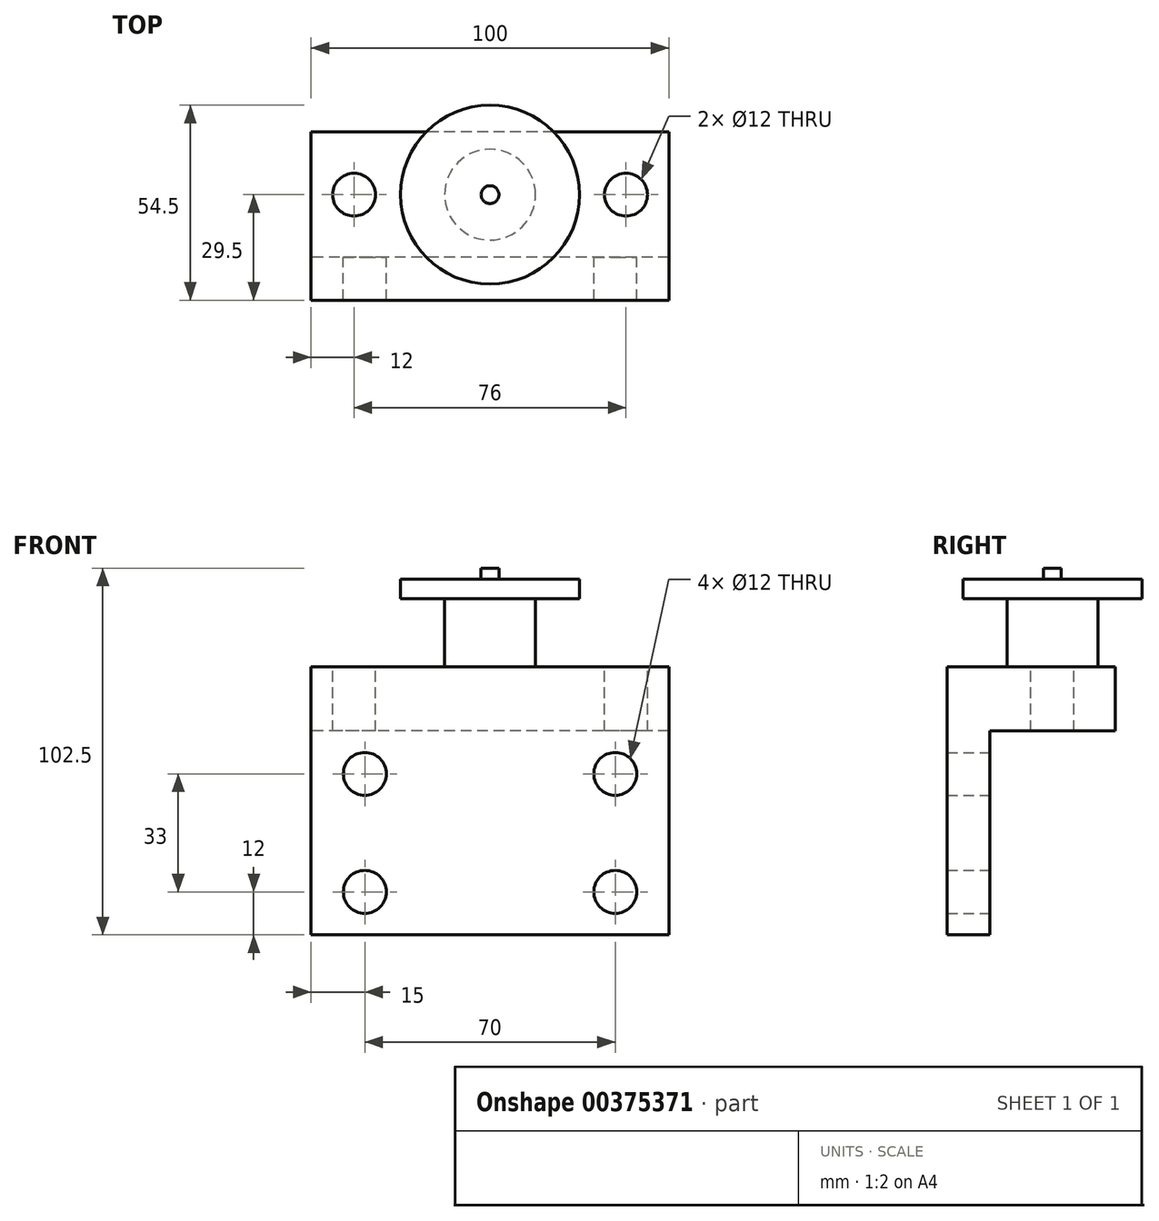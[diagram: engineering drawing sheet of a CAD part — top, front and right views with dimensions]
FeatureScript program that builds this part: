
annotation { "Feature Type Name" : "Feature", "Feature Type Description" : "" }
export const myFeature = defineFeature(function(context is Context, id is Id, definition is map)
    precondition{}
    {
        {
            var Q0;
            Q0=qCreatedBy(makeId("Top.planeOp"),FACE);
            var sketch = newSketch(context, id + "F0", { "sketchPlane" : qUnion([Q0])});
            skLineSegment(sketch, "E0.bottom", {"start": v(50, -17.5) * mm, "end": v(-50, -17.5) * mm});
            skLineSegment(sketch, "E0.top", {"start": v(50, 17.5) * mm, "end": v(-50, 17.5) * mm});
            skLineSegment(sketch, "E0.left", {"start": v(50, -17.5) * mm, "end": v(50, 17.5) * mm});
            skLineSegment(sketch, "E0.right", {"start": v(-50, -17.5) * mm, "end": v(-50, 17.5) * mm});
            skPoint(sketch, "E0.middle", {"position": v(0, 0) * mm});
            skSolve(sketch);
        }
        {
            var Q0;
            Q0=makeQuery(id+"F0.imprint","IMPRINT",FACE,{"disambiguationData":[TD([[makeQuery(id+"F0.imprint","IMPRINT",EDGE,{"derivedFrom":sQuery(id+"F0.wireOp",EDGE,"E0.bottom")}),-1.0]])]});
            extrude(context, id + "F1", {"entities" : qUnion([Q0]), "depth" : -18 * mm});
        }
        {
            var Q0;
            Q0=makeQuery(id+"F1.opExtrude","CAP_FACE",FACE,{"disambiguationData":[OSD([sQuery(id+"F0.wireOp",EDGE,"E0.bottom"),sQuery(id+"F0.wireOp",EDGE,"E0.top"),sQuery(id+"F0.wireOp",EDGE,"E0.left"),sQuery(id+"F0.wireOp",EDGE,"E0.right")])],"isStart":true});
            var sketch = newSketch(context, id + "F2", { "sketchPlane" : qUnion([Q0])});
            skLineSegment(sketch, "E1", {"start": v(50, 0) * mm, "end": v(38, 0) * mm, "construction": true});
            skLineSegment(sketch, "E2", {"start": v(-50, 0) * mm, "end": v(-38, 0) * mm, "construction": true});
            skCircle(sketch, "E3", {"center": v(38, 0) * mm, "radius": 6 * mm});
            skCircle(sketch, "E4", {"center": v(-38, 0) * mm, "radius": 6 * mm});
            skSolve(sketch);
        }
        {
            var Q0;
            Q0=sQuery(id+"F2.wireOp",VERTEX,"E2.end");
            var Q1;
            Q1=sQuery(id+"F2.wireOp",VERTEX,"E3.center");
            var Q2;
            Q2=makeQuery(id+"F1.opExtrude","SWEPT_BODY",BODY,{"disambiguationData":[OSD([sQuery(id+"F0.wireOp",EDGE,"E0.bottom"),sQuery(id+"F0.wireOp",EDGE,"E0.top"),sQuery(id+"F0.wireOp",EDGE,"E0.left"),sQuery(id+"F0.wireOp",EDGE,"E0.right")])]});
            hole(context, id + "F3", {"style" : HoleStyle.SIMPLE, "endStyle" : HoleEndStyle.THROUGH, "holeDiameter" : 12 * mm, "isTappedThrough" : true, "tappedDepth" : 12 * mm, "tapClearance" : 3, "locations" : qUnion([Q0, Q1]), "scope" : qUnion([Q2])});
        }
        {
            var Q0;
            Q0=makeQuery(id+"F1.opExtrude","CAP_FACE",FACE,{"disambiguationData":[OSD([sQuery(id+"F0.wireOp",EDGE,"E0.bottom"),sQuery(id+"F0.wireOp",EDGE,"E0.top"),sQuery(id+"F0.wireOp",EDGE,"E0.left"),sQuery(id+"F0.wireOp",EDGE,"E0.right")])],"isStart":true});
            var sketch = newSketch(context, id + "F4", { "sketchPlane" : qUnion([Q0])});
            skCircle(sketch, "E5", {"center": v(0, 0) * mm, "radius": 12.7 * mm});
            skSolve(sketch);
        }
        {
            var Q0;
            Q0=makeQuery(id+"F4.imprint","IMPRINT",FACE,{"disambiguationData":[TD([[makeQuery(id+"F4.imprint","IMPRINT",EDGE,{"derivedFrom":sQuery(id+"F4.wireOp",EDGE,"E5")}),1.0]])]});
            extrude(context, id + "F5", {"entities" : qUnion([Q0]), "operationType" : NewBodyOperationType.ADD, "depth" : 19 * mm});
        }
        {
            var Q0;
            Q0=makeQuery(id+"F5.opExtrude","CAP_FACE",FACE,{"disambiguationData":[OSD([sQuery(id+"F4.wireOp",EDGE,"E5")])],"isStart":false});
            var sketch = newSketch(context, id + "F6", { "sketchPlane" : qUnion([Q0])});
            skCircle(sketch, "E6", {"center": v(0, 0) * mm, "radius": 25 * mm});
            skSolve(sketch);
        }
        {
            var Q0;
            Q0=makeQuery(id+"F6.imprint","IMPRINT",FACE,{"disambiguationData":[TD([[makeQuery(id+"F6.imprint","IMPRINT",EDGE,{"derivedFrom":sQuery(id+"F6.wireOp",EDGE,"E6")}),1.0]])]});
            var Q1;
            Q1=makeQuery(id+"F6.imprint","IMPRINT",FACE,{"disambiguationData":[TD([[makeQuery(id+"F6.imprint","IMPRINT",EDGE,{"derivedFrom":makeQuery(id+"F5.opExtrude","CAP_EDGE",EDGE,{"disambiguationData":[OSD([sQuery(id+"F4.wireOp",EDGE,"E5")])],"isStart":false})}),1.0]])]});
            extrude(context, id + "F7", {"entities" : qUnion([Q0, Q1]), "operationType" : NewBodyOperationType.ADD, "depth" : 5.5 * mm});
        }
        {
            var Q0;
            Q0=makeQuery(id+"F7.opExtrude","CAP_FACE",FACE,{"disambiguationData":[OSD([sQuery(id+"F6.wireOp",EDGE,"E6")])],"isStart":false});
            var sketch = newSketch(context, id + "F8", { "sketchPlane" : qUnion([Q0])});
            skCircle(sketch, "E7", {"center": v(0, 0) * mm, "radius": 2.5 * mm});
            skSolve(sketch);
        }
        {
            var Q0;
            Q0=qSketchRegion(id+"F8",true);
            extrude(context, id + "F9", {"entities" : qUnion([Q0]), "operationType" : NewBodyOperationType.ADD, "depth" : 3 * mm});
        }
        {
            var Q0;
            Q0=makeQuery(id+"F1.opExtrude","SWEPT_FACE",FACE,{"disambiguationData":[OSD([sQuery(id+"F0.wireOp",EDGE,"E0.bottom")])]});
            var sketch = newSketch(context, id + "F10", { "sketchPlane" : qUnion([Q0])});
            skLineSegment(sketch, "E8.bottom", {"start": v(-50, 0) * mm, "end": v(50, 0) * mm});
            skLineSegment(sketch, "E8.top", {"start": v(-50, -75) * mm, "end": v(50, -75) * mm});
            skLineSegment(sketch, "E8.left", {"start": v(-50, 0) * mm, "end": v(-50, -75) * mm});
            skLineSegment(sketch, "E8.right", {"start": v(50, 0) * mm, "end": v(50, -75) * mm});
            skSolve(sketch);
        }
        {
            var Q0;
            {var subQ0=sQuery(id+"F10.wireOp",EDGE,"E8.top");Q0=makeQuery(id+"F10.imprint","IMPRINT",FACE,{"disambiguationData":[TD([[makeQuery(id+"F10.imprint","IMPRINT",EDGE,{"derivedFrom":subQ0}),1.0]])]});}
            var Q1;
            {var subQ0=sQuery(id+"F10.wireOp",EDGE,"E8.bottom");Q1=makeQuery(id+"F10.imprint","IMPRINT",FACE,{"disambiguationData":[TD([[makeQuery(id+"F10.imprint","IMPRINT",EDGE,{"derivedFrom":subQ0}),1.0]])]});}
            extrude(context, id + "F11", {"entities" : qUnion([Q0, Q1]), "operationType" : NewBodyOperationType.ADD, "depth" : 12 * mm});
        }
        {
            var Q0;
            Q0=makeQuery(id+"F11.opExtrude","CAP_FACE",FACE,{"disambiguationData":[OSD([sQuery(id+"F10.wireOp",EDGE,"E8.bottom"),sQuery(id+"F10.wireOp",EDGE,"E8.top"),sQuery(id+"F10.wireOp",EDGE,"E8.left"),sQuery(id+"F10.wireOp",EDGE,"E8.right")])],"isStart":true});
            var sketch = newSketch(context, id + "F12", { "sketchPlane" : qUnion([Q0])});
            skLineSegment(sketch, "E9", {"start": v(-50, -75) * mm, "end": v(-50, -63) * mm, "construction": true});
            skLineSegment(sketch, "E10", {"start": v(-50, -63) * mm, "end": v(-35, -63) * mm, "construction": true});
            skLineSegment(sketch, "E11", {"start": v(-50, -18) * mm, "end": v(-50, -30) * mm, "construction": true});
            skLineSegment(sketch, "E12", {"start": v(-50, -30) * mm, "end": v(-35, -30) * mm, "construction": true});
            skLineSegment(sketch, "E13", {"start": v(-35, -63) * mm, "end": v(-35, -30) * mm, "construction": true});
            skLineSegment(sketch, "E14", {"start": v(50, -75) * mm, "end": v(50, -63) * mm, "construction": true});
            skLineSegment(sketch, "E15", {"start": v(50, -63) * mm, "end": v(35, -63) * mm, "construction": true});
            skLineSegment(sketch, "E16", {"start": v(50, -18) * mm, "end": v(50, -30) * mm, "construction": true});
            skLineSegment(sketch, "E17", {"start": v(50, -30) * mm, "end": v(35, -30) * mm, "construction": true});
            skSolve(sketch);
        }
        {
            var Q0;
            Q0=sQuery(id+"F12.wireOp",VERTEX,"E13.end");
            var Q1;
            Q1=sQuery(id+"F12.wireOp",VERTEX,"E13.start");
            var Q2;
            Q2=sQuery(id+"F12.wireOp",VERTEX,"E15.end");
            var Q3;
            Q3=sQuery(id+"F12.wireOp",VERTEX,"E17.end");
            var Q4;
            Q4=makeQuery(id+"F1.opExtrude","SWEPT_BODY",BODY,{"disambiguationData":[OSD([sQuery(id+"F0.wireOp",EDGE,"E0.bottom"),sQuery(id+"F0.wireOp",EDGE,"E0.top"),sQuery(id+"F0.wireOp",EDGE,"E0.left"),sQuery(id+"F0.wireOp",EDGE,"E0.right")])]});
            hole(context, id + "F13", {"style" : HoleStyle.SIMPLE, "endStyle" : HoleEndStyle.THROUGH, "holeDiameter" : 12 * mm, "isTappedThrough" : true, "tappedDepth" : 12 * mm, "tapClearance" : 3, "locations" : qUnion([Q0, Q1, Q2, Q3]), "scope" : qUnion([Q4])});
        }
    });
